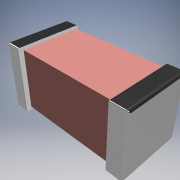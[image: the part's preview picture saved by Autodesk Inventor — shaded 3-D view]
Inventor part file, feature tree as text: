
AUTODESK INVENTOR PART (.ipt)
format: ipt  version: 2016 SP2 (Build 200237200, 237)  size: 231,936 bytes
history: native  units: in
note: dims shown in document units (in); Inventor stores cm internally (conversion verified against a paired STEP export)
features: fillet x2, emboss x1, sketch x1, imported_body x1
ambient origin geometry x8: Origin, YZ Plane, XZ Plane, XY Plane, X Axis, Y Axis, Z Axis, Center Point
bodies: Solid1 (feature_tree)
feature tree (5):
  emboss  "Emboss1"
  fillet  "Fillet1"  Radius=0.0004in
  fillet  "Fillet2"  Radius=0.0004in
  sketch  "Sketch1"  dims[d3=0.001in]
  imported_body  "Base1"
